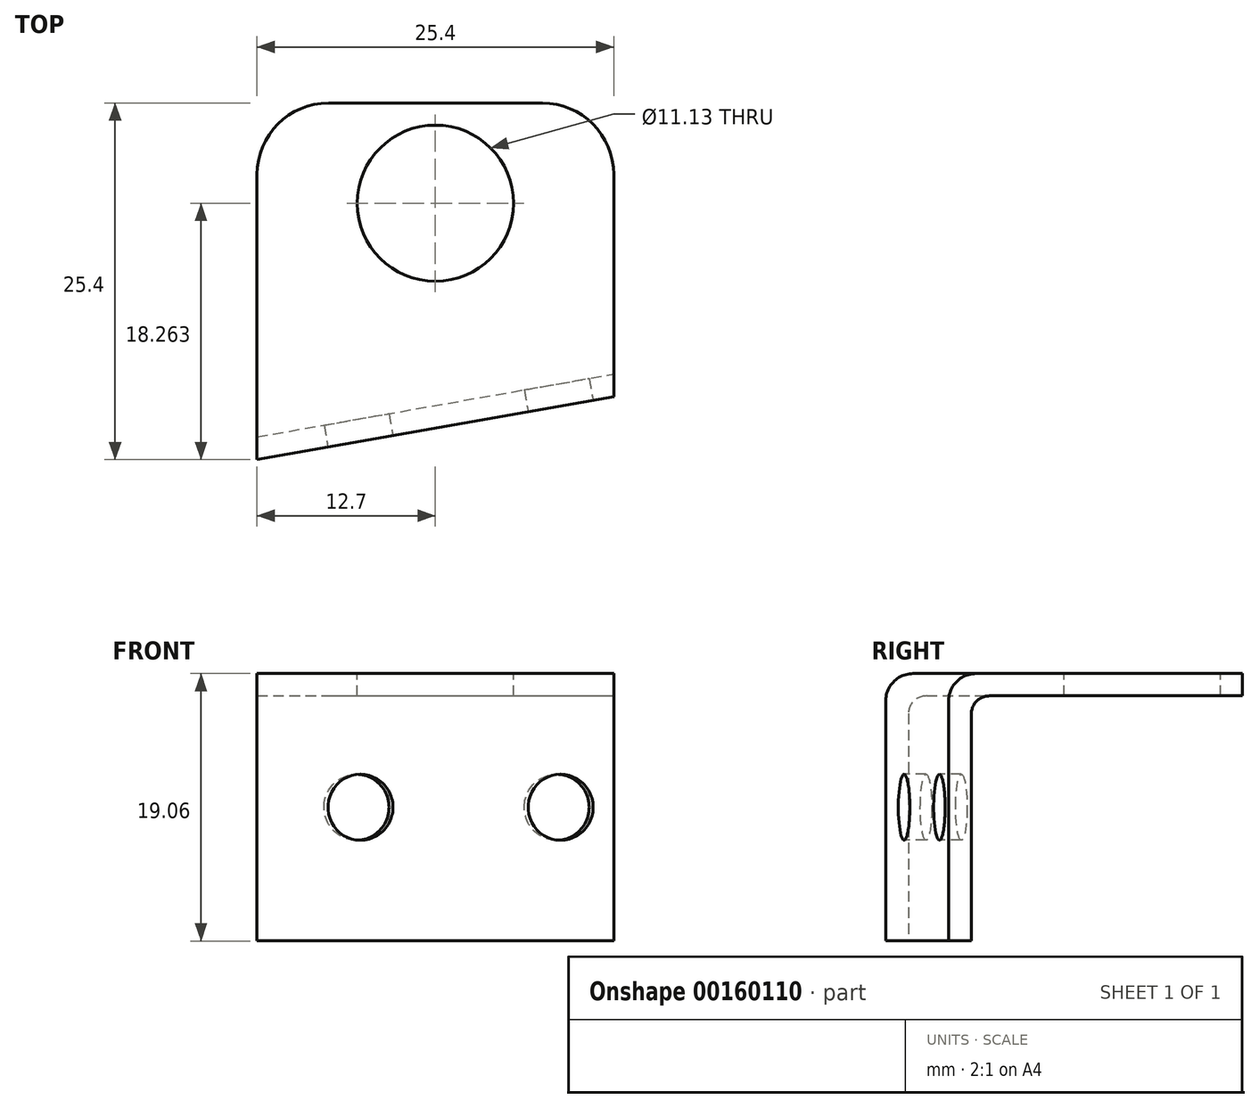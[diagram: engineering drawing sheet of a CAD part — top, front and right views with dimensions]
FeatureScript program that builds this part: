
annotation { "Feature Type Name" : "Feature", "Feature Type Description" : "" }
export const myFeature = defineFeature(function(context is Context, id is Id, definition is map)
    precondition{}
    {
        {
            var Q0;
            Q0=qCreatedBy(makeId("Front.planeOp"),FACE);
            var sketch = newSketch(context, id + "F0", { "sketchPlane" : qUnion([Q0])});
            skLineSegment(sketch, "E0.bottom", {"start": v(-12.7, 9.52) * mm, "end": v(12.7, 9.53) * mm});
            skLineSegment(sketch, "E0.top", {"start": v(-12.7, -9.53) * mm, "end": v(12.7, -9.52) * mm});
            skLineSegment(sketch, "E0.left", {"start": v(-12.7, 9.52) * mm, "end": v(-12.7, -9.53) * mm});
            skLineSegment(sketch, "E0.right", {"start": v(12.7, 9.53) * mm, "end": v(12.7, -9.52) * mm});
            skSolve(sketch);
        }
        {
            var Q0;
            Q0=makeQuery(id+"F0.imprint","IMPRINT",FACE,{"disambiguationData":[TD([[makeQuery(id+"F0.imprint","IMPRINT",EDGE,{"derivedFrom":sQuery(id+"F0.wireOp",EDGE,"E0.bottom")}),-1.0]])]});
            extrude(context, id + "F1", {"entities" : qUnion([Q0]), "endBound" : BoundingType.SYMMETRIC, "depth" : 25.4 * mm});
        }
        {
            var Q0;
            Q0=makeQuery(id+"F1.opExtrude","SWEPT_FACE",FACE,{"disambiguationData":[OSD([sQuery(id+"F0.wireOp",EDGE,"E0.top")])]});
            var sketch = newSketch(context, id + "F2", { "sketchPlane" : qUnion([Q0])});
            skLineSegment(sketch, "E1", {"start": v(-12.7, 12.7) * mm, "end": v(12.7, 8.22) * mm});
            skLineSegment(sketch, "E2", {"start": v(12.7, 8.22) * mm, "end": v(12.7, 12.7) * mm});
            skLineSegment(sketch, "E3", {"start": v(12.7, 12.7) * mm, "end": v(-12.7, 12.7) * mm});
            skLineSegment(sketch, "E4", {"start": v(-12.7, 11.09) * mm, "end": v(12.7, 6.6) * mm});
            skLineSegment(sketch, "E5", {"start": v(-12.7, 11.09) * mm, "end": v(-12.7, -12.7) * mm});
            skLineSegment(sketch, "E6", {"start": v(-12.7, -12.7) * mm, "end": v(12.7, -12.7) * mm});
            skLineSegment(sketch, "E7", {"start": v(12.7, -12.7) * mm, "end": v(12.7, 6.6) * mm});
            skSolve(sketch);
        }
        {
            var Q0;
            Q0=makeQuery(id+"F2.imprint","IMPRINT",FACE,{"disambiguationData":[TD([[makeQuery(id+"F2.imprint","IMPRINT",EDGE,{"derivedFrom":sQuery(id+"F2.wireOp",EDGE,"E1")}),1.0]])]});
            extrude(context, id + "F3", {"entities" : qUnion([Q0]), "operationType" : NewBodyOperationType.REMOVE, "endBound" : BoundingType.THROUGH_ALL, "oppositeDirection" : true, "depth" : 25.4 * mm});
        }
        {
            var Q0;
            Q0=makeQuery(id+"F2.imprint","IMPRINT",FACE,{"disambiguationData":[TD([[makeQuery(id+"F2.imprint","IMPRINT",EDGE,{"derivedFrom":sQuery(id+"F2.wireOp",EDGE,"E4")}),-1.0]])]});
            extrude(context, id + "F4", {"entities" : qUnion([Q0]), "operationType" : NewBodyOperationType.REMOVE, "oppositeDirection" : true, "depth" : 17.46 * mm});
        }
        {
            var Q0;
            Q0=makeQuery(id+"F4.boolean.opBoolean","COPY",EDGE,{"derivedFrom":makeQuery(id+"F4.opExtrude","CAP_EDGE",EDGE,{"disambiguationData":[OSD([sQuery(id+"F2.wireOp",EDGE,"E4")])],"isStart":false})});
            fillet(context, id + "F5", {"entities" : qUnion([Q0]), "radius" : 1.27 * mm, "tangentPropagation" : true, "allowEdgeOverflow" : false});
        }
        {
            var Q0;
            Q0=makeQuery(id+"F3.boolean.opBoolean","INTERSECT",EDGE,{"derivedFrom":[makeQuery(id+"F1.opExtrude","SWEPT_FACE",FACE,{"disambiguationData":[OSD([sQuery(id+"F0.wireOp",EDGE,"E0.bottom")])]}),makeQuery(id+"F3.opExtrude","SWEPT_FACE",FACE,{"disambiguationData":[OSD([sQuery(id+"F2.wireOp",EDGE,"E1")])]})]});
            fillet(context, id + "F6", {"entities" : qUnion([Q0]), "radius" : 1.9 * mm, "tangentPropagation" : true, "allowEdgeOverflow" : false});
        }
        {
            var Q0;
            Q0=makeQuery(id+"F3.boolean.opBoolean","COPY",FACE,{"derivedFrom":makeQuery(id+"F3.opExtrude","SWEPT_FACE",FACE,{"disambiguationData":[OSD([sQuery(id+"F2.wireOp",EDGE,"E1")])]})});
            var sketch = newSketch(context, id + "F7", { "sketchPlane" : qUnion([Q0])});
            skCircle(sketch, "E8", {"center": v(7.24, 0) * mm, "radius": 2.35 * mm});
            skCircle(sketch, "E9", {"center": v(-7.24, 0) * mm, "radius": 2.35 * mm});
            skSolve(sketch);
        }
        {
            var Q0;
            Q0 = qSketchRegion(id + "F7", true);
            extrude(context, id + "F8", {"entities" : qUnion([Q0]), "operationType" : NewBodyOperationType.REMOVE, "endBound" : BoundingType.THROUGH_ALL, "oppositeDirection" : true, "depth" : 25.4 * mm});
        }
        {
            var Q0;
            Q0=makeQuery(id+"F1.opExtrude","SWEPT_FACE",FACE,{"disambiguationData":[OSD([sQuery(id+"F0.wireOp",EDGE,"E0.bottom")])]});
            var sketch = newSketch(context, id + "F9", { "sketchPlane" : qUnion([Q0])});
            skCircle(sketch, "E10", {"center": v(0, 5.56) * mm, "radius": 5.56 * mm});
            skSolve(sketch);
        }
        {
            var Q0;
            Q0=makeQuery(id+"F1.opExtrude","CAP_EDGE",EDGE,{"disambiguationData":[OSD([sQuery(id+"F0.wireOp",EDGE,"E0.right")])],"isStart":true});
            var Q1;
            Q1=makeQuery(id+"F1.opExtrude","CAP_EDGE",EDGE,{"disambiguationData":[OSD([sQuery(id+"F0.wireOp",EDGE,"E0.left")])],"isStart":true});
            fillet(context, id + "F10", {"entities" : qUnion([Q0, Q1]), "radius" : 5.08 * mm, "tangentPropagation" : true, "allowEdgeOverflow" : false});
        }
        {
            var Q0;
            Q0 = qSketchRegion(id + "F9", true);
            extrude(context, id + "F11", {"entities" : qUnion([Q0]), "operationType" : NewBodyOperationType.REMOVE, "endBound" : BoundingType.THROUGH_ALL, "oppositeDirection" : true, "depth" : 25.4 * mm});
        }
    });
